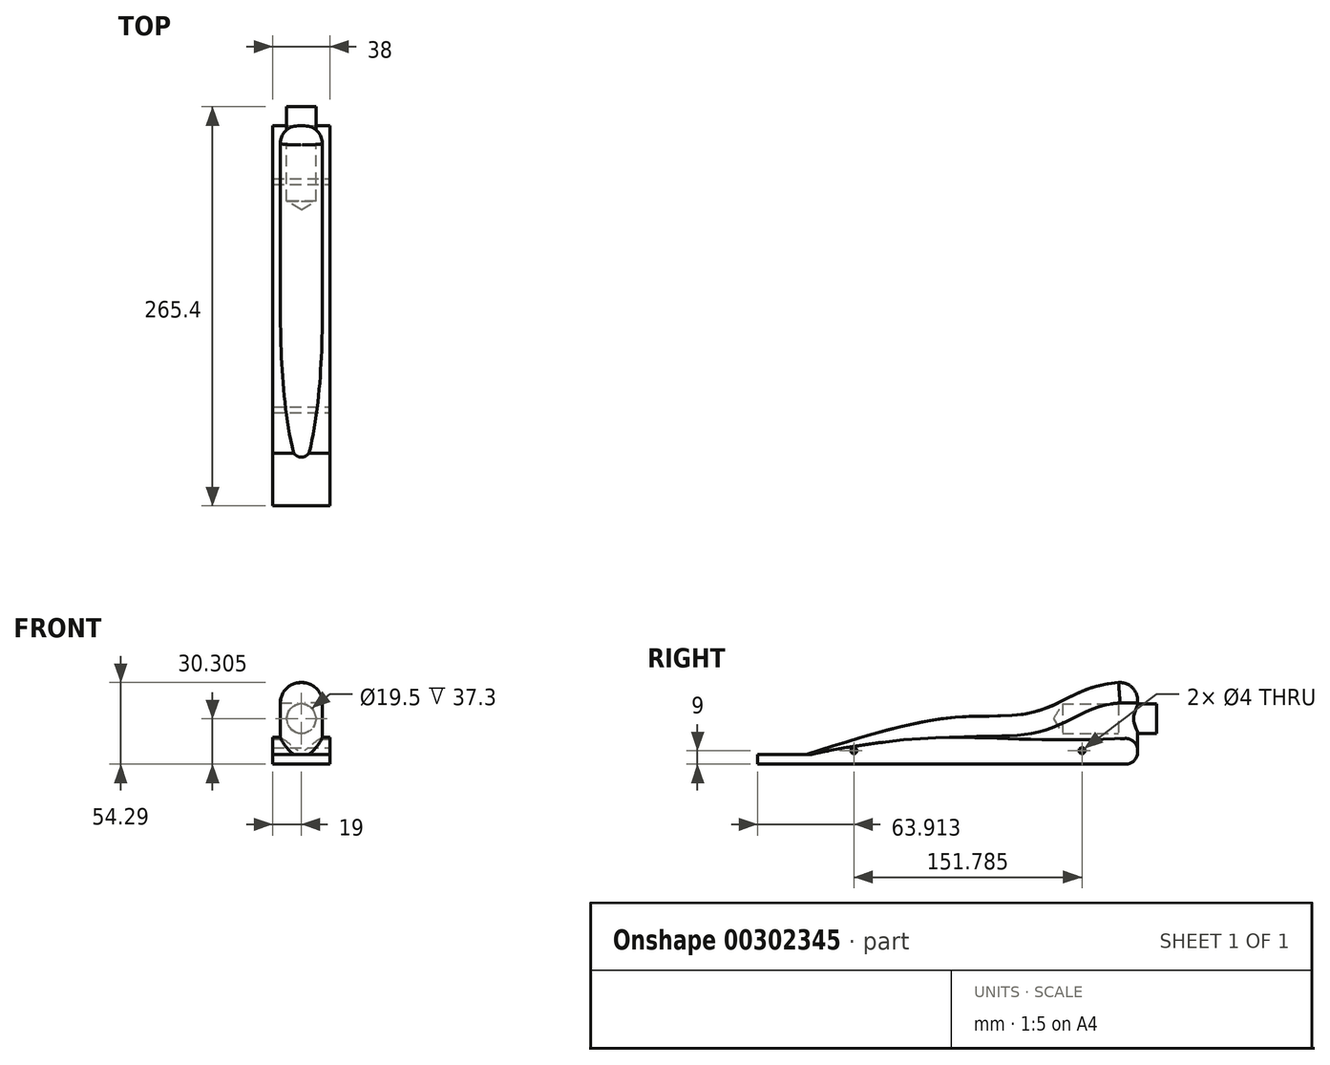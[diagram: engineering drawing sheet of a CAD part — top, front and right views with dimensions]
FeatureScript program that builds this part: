
annotation { "Feature Type Name" : "Feature", "Feature Type Description" : "" }
export const myFeature = defineFeature(function(context is Context, id is Id, definition is map)
    precondition{}
    {
        {
            var Q0;
            Q0=qCreatedBy(makeId("Right.planeOp"),FACE);
            var sketch = newSketch(context, id + "F0", { "sketchPlane" : qUnion([Q0])});
            skLineSegment(sketch, "E0", {"start": v(-76.25, 0) * mm, "end": v(163.75, 0) * mm});
            skLineSegment(sketch, "E1", {"start": v(163.75, 0) * mm, "end": v(163.75, 55) * mm});
            skFitSpline(sketch, "E2", {"points": [v(-76.25, 0) * mm, v(-18.7, 18.22) * mm, v(44.03, 31.31) * mm, v(95.93, 34.92) * mm, v(131.13, 50.27) * mm, v(163.75, 55) * mm], "startDerivative": vector(253.93, 83.81) * mm, "endDerivative": vector(201.7, 8.97) * mm});
            skFitSpline(sketch, "E3", {"points": [v(-76.25, 0) * mm, v(7.89, 16.13) * mm, v(64.4, 17.38) * mm, v(102.2, 16.4) * mm, v(146.94, 16.72) * mm, v(163.75, 16.88) * mm, v(163.75, 16.47) * mm], "startDerivative": vector(148.05, 65.88) * mm, "endDerivative": vector(-8.38, -22.3) * mm});
            skSolve(sketch);
        }
        {
            var Q0;
            {var subQ0=sQuery(id+"F0.wireOp",EDGE,"E1");var subQ1=sQuery(id+"F0.wireOp",EDGE,"E0");var subQ2=makeQuery(id+"F0.imprint","INTERSECT",VERTEX,{"derivedFrom":[subQ1,subQ0]});Q0=makeQuery(id+"F0.imprint","IMPRINT",FACE,{"disambiguationData":[TD([[makeQuery(id+"F0.imprint","IMPRINT",EDGE,{"disambiguationData":[TD([[subQ2,1.0]])],"derivedFrom":subQ1}),1.0]])]});}
            extrude(context, id + "F1", {"entities" : qUnion([Q0]), "depth" : 38 * mm, "offsetDistance" : 25.4 * mm, "symmetric" : true});
        }
        {
            var Q0;
            {var subQ0=sQuery(id+"F0.wireOp",EDGE,"E2");var subQ1=sQuery(id+"F0.wireOp",EDGE,"E1");var subQ2=makeQuery(id+"F0.imprint","INTERSECT",VERTEX,{"derivedFrom":[subQ1,subQ0]});Q0=makeQuery(id+"F0.imprint","IMPRINT",FACE,{"disambiguationData":[TD([[makeQuery(id+"F0.imprint","IMPRINT",EDGE,{"disambiguationData":[TD([[subQ2,1.0]])],"derivedFrom":subQ1}),1.0]])]});}
            extrude(context, id + "F2", {"entities" : qUnion([Q0]), "operationType" : NewBodyOperationType.ADD, "depth" : 27.94 * mm, "offsetDistance" : 25.4 * mm, "symmetric" : true});
        }
        {
            var Q0;
            {var subQ0=sQuery(id+"F0.wireOp",EDGE,"E1");Q0=makeQuery(id+"F2.boolean.opBoolean","MERGE",FACE,{"derivedFrom":[makeQuery(id+"F1.opExtrude","SWEPT_FACE",FACE,{"disambiguationData":[OSD([subQ0])]}),makeQuery(id+"F2.opExtrude","SWEPT_FACE",FACE,{"disambiguationData":[OSD([subQ0])]})]});}
            var sketch = newSketch(context, id + "F3", { "sketchPlane" : qUnion([Q0])});
            skCircle(sketch, "E4", {"center": v(0, 30.3) * mm, "radius": 9.75 * mm});
            skSolve(sketch);
        }
        {
            var Q0;
            Q0=sQuery(id+"F3.wireOp",VERTEX,"E4.center");
            var Q1;
            Q1=makeQuery(id+"F1.opExtrude","SWEPT_BODY",BODY,{"disambiguationData":[OSD([sQuery(id+"F0.wireOp",EDGE,"E0"),sQuery(id+"F0.wireOp",EDGE,"E1"),sQuery(id+"F0.wireOp",EDGE,"E2"),sQuery(id+"F0.wireOp",EDGE,"E3")])]});
            hole(context, id + "F4", {"style" : HoleStyle.SIMPLE, "endStyle" : HoleEndStyle.BLIND, "holeDiameter" : 19.5 * mm, "majorDiameter" : 6.35 * mm, "holeDepth" : 50 * mm, "isTappedThrough" : true, "tappedDepth" : 12.7 * mm, "tapClearance" : 3, "startFromSketch" : true, "locations" : qUnion([Q0]), "scope" : qUnion([Q1])});
        }
        {
            var Q0;
            Q0=makeQuery(id+"F2.opExtrude","CAP_EDGE",EDGE,{"disambiguationData":[OSD([sQuery(id+"F0.wireOp",EDGE,"E2")])],"isStart":false});
            var Q1;
            Q1=makeQuery(id+"F2.opExtrude","CAP_EDGE",EDGE,{"disambiguationData":[OSD([sQuery(id+"F0.wireOp",EDGE,"E2")])],"isStart":true});
            fillet(context, id + "F5", {"entities" : qUnion([Q0, Q1]), "tangentPropagation" : true, "radius" : 13.5 * mm, "defaultsChanged" : true, "vertexSettings" : [], "allowEdgeOverflow" : false});
        }
        {
            var Q0;
            {var subQ0=sQuery(id+"F0.wireOp",EDGE,"E1");Q0=makeQuery(id+"F5.opFillet","BLEND_EDGE",EDGE,{"blendedFrom":[makeQuery(id+"F2.opExtrude","CAP_EDGE",EDGE,{"disambiguationData":[OSD([sQuery(id+"F0.wireOp",EDGE,"E2")])],"isStart":false}),makeQuery(id+"F2.boolean.opBoolean","MERGE",FACE,{"derivedFrom":[makeQuery(id+"F1.opExtrude","SWEPT_FACE",FACE,{"disambiguationData":[OSD([subQ0])]}),makeQuery(id+"F2.opExtrude","SWEPT_FACE",FACE,{"disambiguationData":[OSD([subQ0])]})]})],"blendedInto":[makeQuery(id+"F2.boolean.opBoolean","MERGE",FACE,{"derivedFrom":[makeQuery(id+"F1.opExtrude","SWEPT_FACE",FACE,{"disambiguationData":[OSD([subQ0])]}),makeQuery(id+"F2.opExtrude","SWEPT_FACE",FACE,{"disambiguationData":[OSD([subQ0])]})]})]});}
            var Q1;
            {var subQ0=sQuery(id+"F0.wireOp",EDGE,"E1");Q1=makeQuery(id+"F5.opFillet","BLEND_EDGE",EDGE,{"blendedFrom":[makeQuery(id+"F2.opExtrude","CAP_EDGE",EDGE,{"disambiguationData":[OSD([sQuery(id+"F0.wireOp",EDGE,"E2")])],"isStart":true}),makeQuery(id+"F2.boolean.opBoolean","MERGE",FACE,{"derivedFrom":[makeQuery(id+"F1.opExtrude","SWEPT_FACE",FACE,{"disambiguationData":[OSD([subQ0])]}),makeQuery(id+"F2.opExtrude","SWEPT_FACE",FACE,{"disambiguationData":[OSD([subQ0])]})]})],"blendedInto":[makeQuery(id+"F2.boolean.opBoolean","MERGE",FACE,{"derivedFrom":[makeQuery(id+"F1.opExtrude","SWEPT_FACE",FACE,{"disambiguationData":[OSD([subQ0])]}),makeQuery(id+"F2.opExtrude","SWEPT_FACE",FACE,{"disambiguationData":[OSD([subQ0])]})]})]});}
            var Q2;
            Q2=makeQuery(id+"F2.opExtrude","CAP_EDGE",EDGE,{"disambiguationData":[OSD([sQuery(id+"F0.wireOp",EDGE,"E1")])],"isStart":true});
            var Q3;
            Q3=makeQuery(id+"F2.opExtrude","CAP_EDGE",EDGE,{"disambiguationData":[OSD([sQuery(id+"F0.wireOp",EDGE,"E1")])],"isStart":false});
            fillet(context, id + "F6", {"entities" : qUnion([Q0, Q1, Q2, Q3]), "tangentPropagation" : true, "radius" : 11.65 * mm, "defaultsChanged" : false, "vertexSettings" : [], "allowEdgeOverflow" : false});
        }
        {
            var Q0;
            {var subQ0=sQuery(id+"F0.wireOp",EDGE,"E1");var subQ1=sQuery(id+"F0.wireOp",EDGE,"E3");var subQ2=sQuery(id+"F0.wireOp",EDGE,"E2");Q0=makeQuery(id+"F2.boolean.opBoolean","SPLIT",EDGE,{"disambiguationData":[TD([makeQuery(id+"F2.opExtrude","CAP_FACE",FACE,{"disambiguationData":[OSD([subQ0,subQ2,subQ1])],"isStart":false})])],"derivedFrom":makeQuery(id+"F1.opExtrude","SWEPT_EDGE",EDGE,{"disambiguationData":[OSD([subQ0,subQ1])]})});}
            var Q1;
            {var subQ0=sQuery(id+"F0.wireOp",EDGE,"E3");var subQ1=sQuery(id+"F0.wireOp",EDGE,"E2");var subQ2=sQuery(id+"F0.wireOp",EDGE,"E1");Q1=makeQuery(id+"F2.boolean.opBoolean","SPLIT",EDGE,{"disambiguationData":[TD([makeQuery(id+"F2.opExtrude","CAP_FACE",FACE,{"disambiguationData":[OSD([subQ2,subQ1,subQ0])],"isStart":true})])],"derivedFrom":makeQuery(id+"F1.opExtrude","SWEPT_EDGE",EDGE,{"disambiguationData":[OSD([subQ2,subQ0])]})});}
            var Q2;
            Q2=makeQuery(id+"F1.opExtrude","SWEPT_EDGE",EDGE,{"disambiguationData":[OSD([sQuery(id+"F0.wireOp",EDGE,"E0"),sQuery(id+"F0.wireOp",EDGE,"E1")])]});
            fillet(context, id + "F7", {"entities" : qUnion([Q0, Q1, Q2]), "tangentPropagation" : true, "radius" : 7.97 * mm, "defaultsChanged" : true, "vertexSettings" : [], "allowEdgeOverflow" : false});
        }
        {
            var Q0;
            Q0=makeQuery(id+"F1.opExtrude","CAP_FACE",FACE,{"disambiguationData":[OSD([sQuery(id+"F0.wireOp",EDGE,"E0"),sQuery(id+"F0.wireOp",EDGE,"E1"),sQuery(id+"F0.wireOp",EDGE,"E2"),sQuery(id+"F0.wireOp",EDGE,"E3")])],"isStart":false});
            var sketch = newSketch(context, id + "F8", { "sketchPlane" : qUnion([Q0])});
            skCircle(sketch, "E5", {"center": v(-25.04, 9) * mm, "radius": 2 * mm});
            skCircle(sketch, "E6", {"center": v(126.75, 9) * mm, "radius": 2 * mm});
            skSolve(sketch);
        }
        {
            var Q0;
            Q0=sQuery(id+"F8.wireOp",VERTEX,"E5.center");
            var Q1;
            Q1=sQuery(id+"F8.wireOp",VERTEX,"E6.center");
            var Q2;
            Q2=makeQuery(id+"F1.opExtrude","SWEPT_BODY",BODY,{"disambiguationData":[OSD([sQuery(id+"F0.wireOp",EDGE,"E0"),sQuery(id+"F0.wireOp",EDGE,"E1"),sQuery(id+"F0.wireOp",EDGE,"E2"),sQuery(id+"F0.wireOp",EDGE,"E3")])]});
            hole(context, id + "F9", {"style" : HoleStyle.SIMPLE, "endStyle" : HoleEndStyle.BLIND, "holeDiameter" : 4 * mm, "majorDiameter" : 6.35 * mm, "holeDepth" : 50 * mm, "isTappedThrough" : true, "tappedDepth" : 12.7 * mm, "tapClearance" : 3, "startFromSketch" : true, "locations" : qUnion([Q0, Q1]), "scope" : qUnion([Q2])});
        }
        {
            var Q0;
            {var subQ0=sQuery(id+"F0.wireOp",EDGE,"E1");Q0=makeQuery(id+"F6.opFillet","SPLIT",FACE,{"disambiguationData":[OD(0.0)],"derivedFrom":makeQuery(id+"F2.boolean.opBoolean","MERGE",FACE,{"derivedFrom":[makeQuery(id+"F1.opExtrude","SWEPT_FACE",FACE,{"disambiguationData":[OSD([subQ0])]}),makeQuery(id+"F2.opExtrude","SWEPT_FACE",FACE,{"disambiguationData":[OSD([subQ0])]})]})});}
            cPlane(context, id + "F10", {"entities" : qUnion([Q0]), "cplaneType" : CPlaneType.OFFSET, "offset" : 0 * mm, "width" : 152.4 * mm, "height" : 152.4 * mm});
        }
        {
            var Q0;
            Q0=qCreatedBy(id+"F10.planeOp",FACE);
            var sketch = newSketch(context, id + "F11", { "sketchPlane" : qUnion([Q0])});
            skArc(sketch, "E7.0", {"start": v(-2.32, 39.77) * mm, "mid": v(-9.75, 30.3) * mm, "end": v(-2.32, 20.83) * mm});
            skArc(sketch, "E8.0", {"start": v(2.32, 20.83) * mm, "mid": v(9.75, 30.3) * mm, "end": v(2.32, 39.77) * mm});
            skArc(sketch, "E9.0", {"start": v(-2.32, 20.83) * mm, "mid": v(0, 20.55) * mm, "end": v(2.32, 20.83) * mm});
            skArc(sketch, "E10.0", {"start": v(2.32, 39.77) * mm, "mid": v(0, 40.05) * mm, "end": v(-2.32, 39.77) * mm});
            skSolve(sketch);
        }
        {
            var Q0;
            Q0 = qSketchRegion(id + "F11", true);
            extrude(context, id + "F12", {"entities" : qUnion([Q0]), "operationType" : NewBodyOperationType.ADD, "depth" : 25.4 * mm, "offsetDistance" : 25.4 * mm, "symmetric" : true});
        }
        {
            var Q0;
            Q0=makeQuery(id+"F1.opExtrude","SWEPT_EDGE",EDGE,{"disambiguationData":[OSD([sQuery(id+"F0.wireOp",EDGE,"E0"),sQuery(id+"F0.wireOp",EDGE,"E2"),sQuery(id+"F0.wireOp",EDGE,"E3")])]});
            cPoint(context, id + "F13", {"entities" : qUnion([Q0]), "parameter" : 0.5});
        }
        {
            var Q0;
            Q0=qCreatedBy(makeId("Front.planeOp"),FACE);
            var Q1;
            Q1 = qCreatedBy(id + "F13" ,VERTEX);
            cPlane(context, id + "F14", {"entities" : qUnion([Q0, Q1]), "cplaneType" : CPlaneType.PLANE_POINT, "offset" : 25.4 * mm, "width" : 152.4 * mm, "height" : 152.4 * mm});
        }
        {
            var Q0;
            Q0=qCreatedBy(id+"F14.planeOp",FACE);
            var sketch = newSketch(context, id + "F15", { "sketchPlane" : qUnion([Q0])});
            skPoint(sketch, "E11.0", {"position": v(-19, 0) * mm});
            skPoint(sketch, "E12.0", {"position": v(19, 0) * mm});
            skLineSegment(sketch, "E13.bottom", {"start": v(-19, 0) * mm, "end": v(19, 0) * mm});
            skLineSegment(sketch, "E13.top", {"start": v(-19, 6.48) * mm, "end": v(19, 6.48) * mm});
            skLineSegment(sketch, "E13.left", {"start": v(-19, 0) * mm, "end": v(-19, 6.48) * mm});
            skLineSegment(sketch, "E13.right", {"start": v(19, 0) * mm, "end": v(19, 6.48) * mm});
            skSolve(sketch);
        }
        {
            var Q0;
            Q0 = qSketchRegion(id + "F15", true);
            extrude(context, id + "F16", {"entities" : qUnion([Q0]), "operationType" : NewBodyOperationType.ADD, "depth" : 12.7 * mm, "offsetDistance" : 25.4 * mm});
        }
        {
            var Q0;
            Q0 = qSketchRegion(id + "F15", true);
            extrude(context, id + "F17", {"entities" : qUnion([Q0]), "operationType" : NewBodyOperationType.ADD, "oppositeDirection" : true, "depth" : 25.4 * mm, "offsetDistance" : 25.4 * mm});
        }
    });
